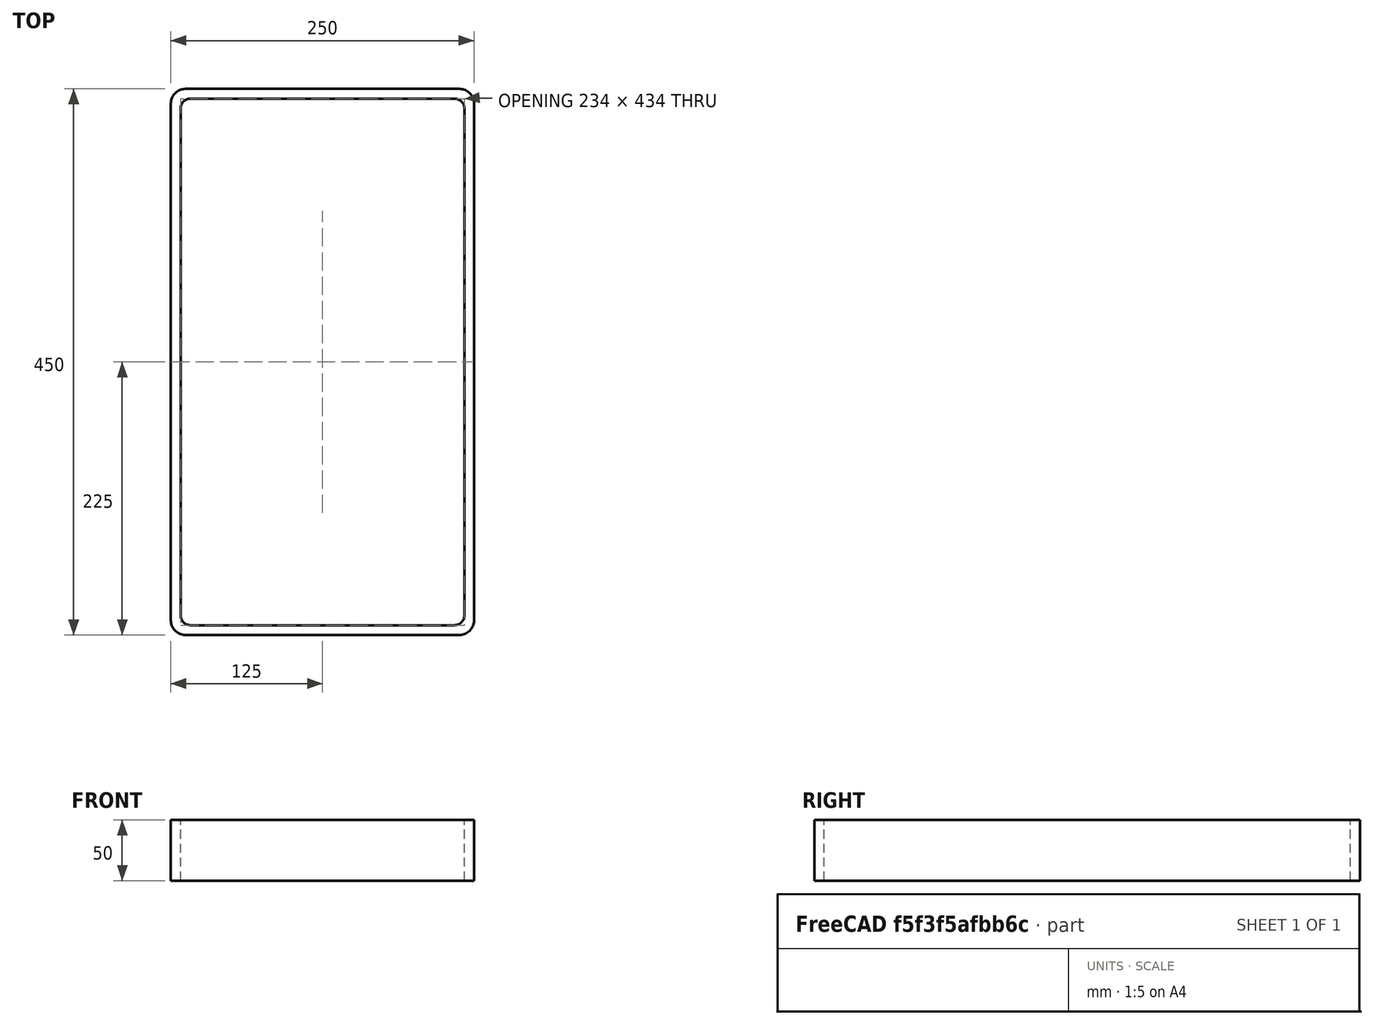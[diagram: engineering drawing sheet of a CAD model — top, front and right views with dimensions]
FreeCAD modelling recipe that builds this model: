
FCSTD DOCUMENT  (FreeCAD 0.15R4671 (Git))
Label: Rectangular hollow section 450x250x8 EN10219 S235JRH
License: All rights reserved
LicenseURL: http://en.wikipedia.org/wiki/All_rights_reserved
objects: Sketcher::SketchObject×1, Part::Extrusion×1
note: 2 computed .brp shape members not serialized (recipe doc carries the construction recipe); baked Part::Feature solids carry a one-line shape summary decoded from their .brp

FEATURE [Sketcher::SketchObject] Sketch
  sketch-geometry (16):
    g0: LineSegment StartX=-109 StartY=217 StartZ=0 EndX=109 EndY=217 EndZ=0
    g1: LineSegment StartX=117 StartY=209 StartZ=0 EndX=117 EndY=-209 EndZ=0
    g2: LineSegment StartX=109 StartY=-217 StartZ=0 EndX=-109 EndY=-217 EndZ=0
    g3: LineSegment StartX=-117 StartY=-209 StartZ=0 EndX=-117 EndY=209 EndZ=0
    g4: LineSegment StartX=-113 StartY=225 StartZ=0 EndX=113 EndY=225 EndZ=0
    g5: LineSegment StartX=125 StartY=213 StartZ=0 EndX=125 EndY=-213 EndZ=0
    g6: LineSegment StartX=113 StartY=-225 StartZ=0 EndX=-113 EndY=-225 EndZ=0
    g7: LineSegment StartX=-125 StartY=-213 StartZ=0 EndX=-125 EndY=213 EndZ=0
    g8: ArcOfCircle CenterX=-109 CenterY=209 CenterZ=0 NormalX=0 NormalY=0 NormalZ=1 Radius=8 StartAngle=1.5708 EndAngle=3.14159
    g9: ArcOfCircle CenterX=109 CenterY=209 CenterZ=0 NormalX=0 NormalY=0 NormalZ=1 Radius=8 StartAngle=0 EndAngle=1.5708
    g10: ArcOfCircle CenterX=109 CenterY=-209 CenterZ=0 NormalX=0 NormalY=0 NormalZ=1 Radius=8 StartAngle=4.71239 EndAngle=6.28319
    g11: ArcOfCircle CenterX=-109 CenterY=-209 CenterZ=0 NormalX=0 NormalY=0 NormalZ=1 Radius=8 StartAngle=3.14159 EndAngle=4.71239
    g12: ArcOfCircle CenterX=113 CenterY=213 CenterZ=0 NormalX=0 NormalY=0 NormalZ=1 Radius=12 StartAngle=0 EndAngle=1.5708
    g13: ArcOfCircle CenterX=113 CenterY=-213 CenterZ=0 NormalX=0 NormalY=0 NormalZ=1 Radius=12 StartAngle=4.71239 EndAngle=6.28319
    g14: ArcOfCircle CenterX=-113 CenterY=-213 CenterZ=0 NormalX=0 NormalY=0 NormalZ=1 Radius=12 StartAngle=3.14159 EndAngle=4.71239
    g15: ArcOfCircle CenterX=-113 CenterY=213 CenterZ=0 NormalX=0 NormalY=0 NormalZ=1 Radius=12 StartAngle=1.5708 EndAngle=3.14159
  constraints (36):
    c: Horizontal(g2)
    c: Vertical(g3)
    c: Horizontal(g6)
    c: Vertical(g7)
    c: Tangent(g3,g8) = 1.5708
    c: Tangent(g0,g8) = 1.5708
    c: Tangent(g0,g9) = 1.5708
    c: Tangent(g1,g9) = 1.5708
    c: Tangent(g1,g10) = 1.5708
    c: Tangent(g2,g10) = 1.5708
    c: Tangent(g2,g11) = 1.5708
    c: Tangent(g3,g11) = 1.5708
    c: Tangent(g4,g12) = 1.5708
    c: Tangent(g5,g12) = 1.5708
    c: Tangent(g5,g13) = 1.5708
    c: Tangent(g6,g13) = 1.5708
    c: Tangent(g6,g14) = 1.5708
    c: Tangent(g7,g14) = 1.5708
    c: Tangent(g7,g15) = 1.5708
    c: Tangent(g4,g15) = 1.5708
    c: Equal(g9,g8)
    c: Equal(g9,g11)
    c: Equal(g9,g10)
    c: Equal(g12,g15)
    c: Equal(g12,g14)
    c: Equal(g12,g13)
    c: Symmetric(g4,g6,g-1)
    c: Symmetric(g7,g5,g-2)
    c: DistanceY(g4,g6) = -450
    c: DistanceX(g7,g5) = 250
    c: Symmetric(g3,g1,g-2)
    c: Symmetric(g0,g2,g-1)
    c: DistanceY(g0,g4) = 8
    c: DistanceX(g5,g1) = -8
    c: Radius(g9) = 8
    c: Radius(g12) = 12
FEATURE [Part::Extrusion] Extrude  label="Rectangular hollow section 450x250x8 EN10219 S235JRH"
  Base = -> Sketch
  Dir = (0,0,50)
  Solid = true
